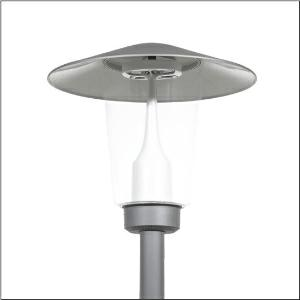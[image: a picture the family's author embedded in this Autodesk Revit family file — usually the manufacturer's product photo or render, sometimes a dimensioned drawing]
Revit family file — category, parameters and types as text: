
# Revit family: pilzleuchte_iq___p1_0a_5xa5235nf14hp_8191
name_source: partatom
category: Lighting Fixtures
units: mm (PartAtom-declared; Revit-internal decimal feet)

## family parameters
Cut with Voids When Loaded = No
Host = Face
Light Source = No
Part Type = Normal
Room Calculation Point = No
Round Connector Dimension = Use Diameter
Shared = No

## types (1)
- --- (1 x LED, 4250 lm, 33.6 W, 2700K)
    Apparent Load = 34 VA
    CIE Flux Codes = 35 64 90 96 100
    Color Rendering = 70
    Color Temperature = 2700K
    Default Elevation = 1800 mm
    Description = Mushroom Luminaire iQ, mast luminaire, Module 540 iQ-SR, primary light control with 3 zone facetted reflector, of plastic, silver coated, highly specular, structured, primary optical cover: cover, of PMMA, transparent, light distribution: P1.0a, light emission: direct distribution, primary light characteristic: strongly asymmetric, installation type: post-top, LED, High Power LED, rated luminous flux: 4.250lm, luminous efficacy: 127lm/W, light colour: 727, colour temperature: 2700K, control gear: iQ Street-Remote, control: pre-setting: logarithmic dimming characteristic, Street-Remote, Auto-Match, Temp-Guard, Lumen-Switch, Night-Set, Smart-Wire, Light-Fading, Desk-Remote (wireless, voltage-free reading and setting of iQ features in the workshop via application-optimized NFC function/RFID function), optimised constant luminous flux control (CLO 2.0), with terminal, 6-pole, max. 2.5mm², mains connection: 230..240V, AC, 50/60Hz, start of lifetime: 34W, end of service life: 36W, reduction: 15W, luminaire housing, upper part, of glass-fibre reinforced polyester, coated, Siteco® metallic grey (DB 702S), diameter: 650mm, height: 586mm, spigot size: d x l = 76 x 70mm (post-top) | with reducer (optional accessory) 60 x 70mm, mounting height: 3..5m, post-top mast mounting element, of diecast aluminium, coated, Siteco® metallic grey (DB 702S), Module 540 iQ-SR, traffic white (RAL 9016), equipment: Power, protection rating (complete): IP65, insulation class (complete): insulation class II (safety insulation), certification: CE, ENEC, VDE, packaging unit: 1 piece

Light Distribution: P1.0a
    Height = 586 mm
    Lamp = 1 x LED
    Lamp Light Flux = 4250 lm
    Lamp Power = 33.6 W
    Lamp count = 1
    Length = 650 mm
    Luminous efficacy = 126 lm/W
    Manufacturer = Siteco
    ModVariant = No
    Model = 5XA5235NF14HP
    Mounting Place = Pole
    Mounting Type = Pole top
    Number of Poles = 1
    OnlyDefault = Yes
    Power Factor = 1
    Product Name = Pilzleuchte iQ | P1.0a
    Product group = mast luminaire | pylon top
    ProductGroupID = 6100
    Protection Class = Protection class II
    Protection Degree = IP 65
    RLX_Detail_Level = 1
    RLX_Emergency_Light_Flux = 0 lm
    RLX_Emergency_Type = 0
    RLX_Emergency_Type_DB = No
    RlxData = <blob elided: 51913 chars, md5=391fa804>
    Socket = socket
    Standby Power = 0 W
    System Light Flux = 4250 lm
    System Power = 34 W
    Type Comments = factory setting: luminous flux: 100 % | dim-lin: 254 | 695 mA
    Type Image = l_1006077.jpg
    URL = http://relux.com
    VarID = @adj_153335
    Voltage = 0 V
    Weight = 0.00 kg
    Width = 0 mm  [stored 0 ft]

note: [stored X ft] marks values corroborated as IEEE doubles in the binary element streams (Revit-internal decimal feet)

## geometry (parser evidence)
native form markers: Blend x4, Sweep x11
no freeform markers — native parametric forms only
